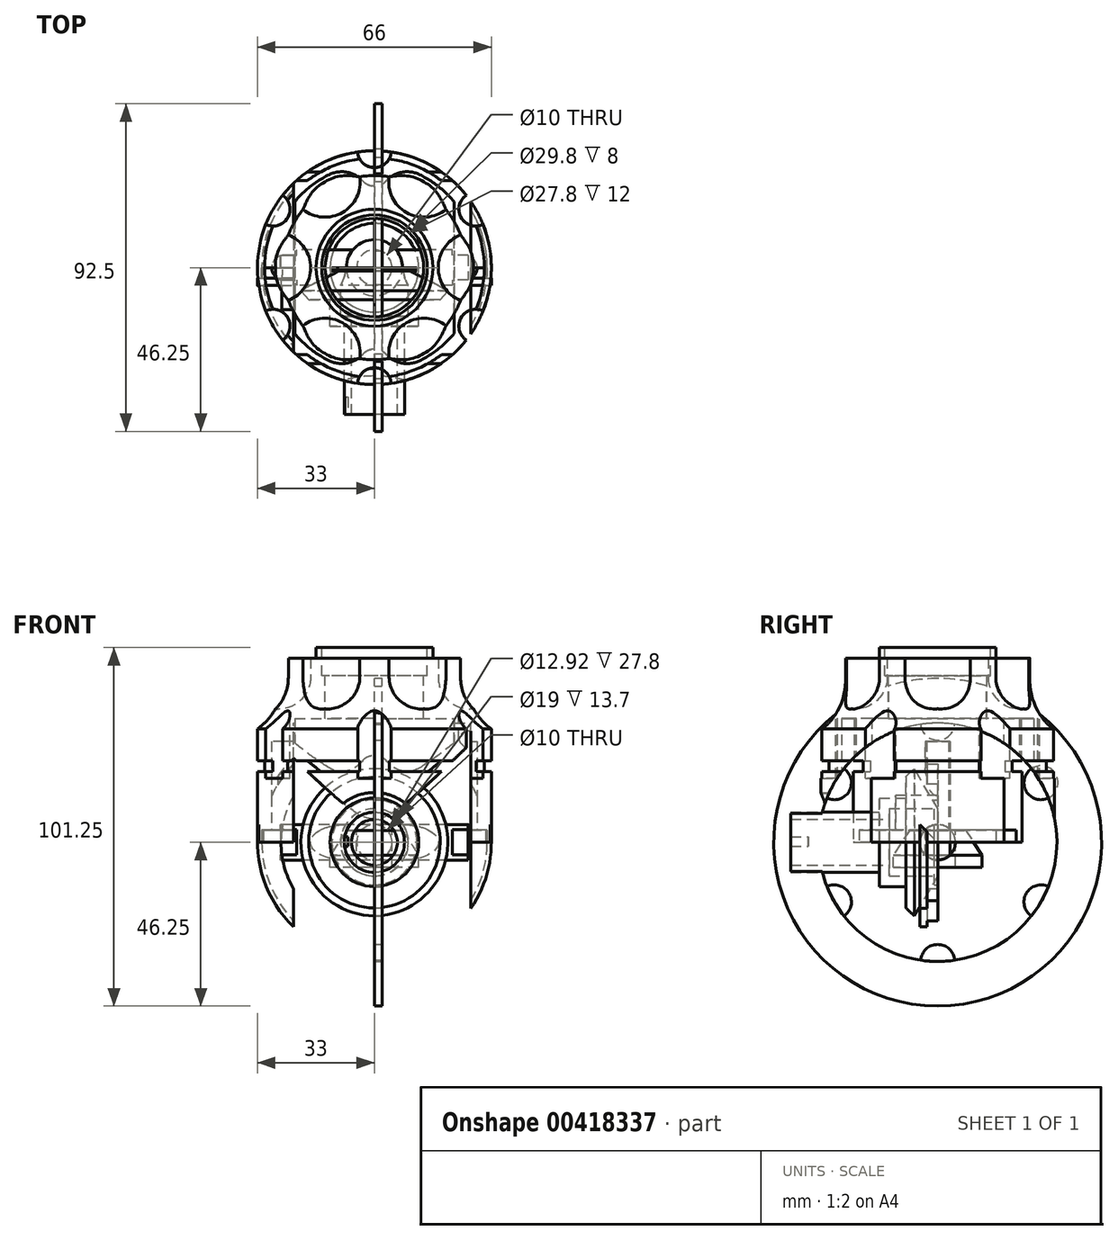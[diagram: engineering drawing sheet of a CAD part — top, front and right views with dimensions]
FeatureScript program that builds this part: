
annotation { "Feature Type Name" : "Feature", "Feature Type Description" : "" }
export const myFeature = defineFeature(function(context is Context, id is Id, definition is map)
    precondition{}
    {
        {
            var Q0;
            Q0=qCreatedBy(makeId("Top.planeOp"),FACE);
            var sketch = newSketch(context, id + "F0", { "sketchPlane" : qUnion([Q0])});
            skCircle(sketch, "E0", {"center": v(0, 0) * mm, "radius": 33 * mm});
            skSolve(sketch);
        }
        {
            var Q0;
            Q0=makeQuery(id+"F0.imprint","IMPRINT",FACE,{"disambiguationData":[TD([[makeQuery(id+"F0.imprint","IMPRINT",EDGE,{"derivedFrom":sQuery(id+"F0.wireOp",EDGE,"E0")}),1.0]])]});
            extrude(context, id + "F1", {"entities" : qUnion([Q0]), "depth" : 52 * mm});
        }
        {
            var Q0;
            Q0=qCreatedBy(makeId("Front.planeOp"),FACE);
            var sketch = newSketch(context, id + "F2", { "sketchPlane" : qUnion([Q0])});
            skFitSpline(sketch, "E1", {"points": [v(26, 52) * mm, v(26, 47.04) * mm, v(33, 32) * mm], "startDerivative": vector(0, -19.9) * mm, "endDerivative": vector(32.48, -23.97) * mm});
            skFitSpline(sketch, "E2", {"points": [v(26, 52) * mm, v(48.34, 55.62) * mm, v(50, 40.52) * mm, v(33, 32) * mm], "startDerivative": vector(76.47, 62.5) * mm, "endDerivative": vector(-112.87, -110.3) * mm});
            skLineSegment(sketch, "E3", {"start": v(33, 68.61) * mm, "end": v(33, -35.09) * mm, "construction": true});
            skLineSegment(sketch, "E4", {"start": v(26, 67.83) * mm, "end": v(26, -39.5) * mm, "construction": true});
            skLineSegment(sketch, "E5", {"start": v(-64.2, 52) * mm, "end": v(63.42, 52) * mm, "construction": true});
            skLineSegment(sketch, "E6", {"start": v(0, 62.64) * mm, "end": v(0, -36.65) * mm, "construction": true});
            skSolve(sketch);
        }
        {
            var Q0;
            Q0=makeQuery(id+"F2.imprint","IMPRINT",FACE,{"disambiguationData":[TD([[makeQuery(id+"F2.imprint","IMPRINT",EDGE,{"derivedFrom":sQuery(id+"F2.wireOp",EDGE,"E1")}),1.0]])]});
            var Q1;
            Q1=sQuery(id+"F2.wireOp",EDGE,"E6");
            revolve(context, id + "F3", {"operationType" : NewBodyOperationType.REMOVE, "entities" : qUnion([Q0]), "axis" : qUnion([Q1]), "revolveType" : RevolveType.FULL, "oppositeDirection" : true});
        }
        {
            var Q0;
            Q0=qCreatedBy(makeId("Front.planeOp"),FACE);
            var sketch = newSketch(context, id + "F4", { "sketchPlane" : qUnion([Q0])});
            skLineSegment(sketch, "E7", {"start": v(26, 80.97) * mm, "end": v(26, -38.86) * mm, "construction": true});
            skLineSegment(sketch, "E8", {"start": v(18, 70.17) * mm, "end": v(18, -34.83) * mm, "construction": true});
            skLineSegment(sketch, "E9", {"start": v(-52.24, 52) * mm, "end": v(60.82, 52) * mm, "construction": true});
            skFitSpline(sketch, "E10", {"points": [v(26, 52) * mm, v(26, 49.65) * mm, v(26, 47.35) * mm, v(26, 37.17) * mm, v(33, 32) * mm]});
            skFitSpline(sketch, "E11", {"points": [v(-33, 32) * mm, v(-26, 37.17) * mm, v(-26, 47.35) * mm, v(-26, 49.65) * mm, v(-26, 52) * mm]});
            skFitSpline(sketch, "E12", {"points": [v(26, 52) * mm, v(26, 49.65) * mm, v(26, 47.35) * mm, v(26, 37.17) * mm, v(33, 32) * mm]});
            skFitSpline(sketch, "E13", {"points": [v(-33, 32) * mm, v(-26, 37.17) * mm, v(-26, 47.35) * mm, v(-26, 49.65) * mm, v(-26, 52) * mm]});
            skLineSegment(sketch, "E14", {"start": v(18, 52) * mm, "end": v(18, 46.65) * mm});
            skPoint(sketch, "E15", {"position": v(27.95, 37.7) * mm});
            skArc(sketch, "E16", {"start": v(18, 46.65) * mm, "mid": v(20.98, 39.96) * mm, "end": v(27.95, 37.7) * mm});
            skLineSegment(sketch, "E17", {"start": v(27.95, 37.7) * mm, "end": v(27.95, 52) * mm});
            skLineSegment(sketch, "E18", {"start": v(27.95, 52) * mm, "end": v(18, 52) * mm});
            skLineSegment(sketch, "E19", {"start": v(27.95, 56.84) * mm, "end": v(27.95, 25.56) * mm, "construction": true});
            skLineSegment(sketch, "E20", {"start": v(0, 68.38) * mm, "end": v(0, -25.66) * mm, "construction": true});
            skSolve(sketch);
        }
        {
            var Q0;
            Q0 = qSketchRegion(id + "F4", true);
            var Q1;
            Q1=sQuery(id+"F4.wireOp",EDGE,"E19");
            revolve(context, id + "F5", {"entities" : qUnion([Q0]), "axis" : qUnion([Q1]), "revolveType" : RevolveType.FULL, "oppositeDirection" : true});
        }
        {
            var Q0;
            Q0=makeQuery(id+"F5.opRevolve","SWEPT_BODY",BODY,{"disambiguationData":[OSD([sQuery(id+"F4.wireOp",EDGE,"E14"),sQuery(id+"F4.wireOp",EDGE,"E16"),sQuery(id+"F4.wireOp",EDGE,"E17"),sQuery(id+"F4.wireOp",EDGE,"E18")])]});
            var Q1;
            Q1=sQuery(id+"F4.wireOp",EDGE,"E20");
            circularPattern(context, id + "F6", {"operationType" : NewBodyOperationType.REMOVE, "entities" : qUnion([Q0]), "axis" : qUnion([Q1]), "angle" : 360 * degree, "instanceCount" : 6, "equalSpace" : true});
        }
        {
            var Q0;
            Q0=qCreatedBy(makeId("Front.planeOp"),FACE);
            cPlane(context, id + "F7", {"entities" : qUnion([Q0]), "cplaneType" : CPlaneType.OFFSET, "offset" : 33 * mm, "width" : 150 * mm, "height" : 150 * mm});
        }
        {
            var Q0;
            Q0=qCreatedBy(id+"F7.planeOp",FACE);
            var sketch = newSketch(context, id + "F8", { "sketchPlane" : qUnion([Q0])});
            skLineSegment(sketch, "E21.bottom", {"start": v(0, 41.84) * mm, "end": v(4.75, 41.84) * mm});
            skLineSegment(sketch, "E21.top", {"start": v(0, 18) * mm, "end": v(4.75, 18) * mm});
            skLineSegment(sketch, "E21.left", {"start": v(0, 41.84) * mm, "end": v(0, 18) * mm});
            skLineSegment(sketch, "E21.right", {"start": v(4.75, 41.84) * mm, "end": v(4.75, 18) * mm});
            skLineSegment(sketch, "E22", {"start": v(0, 61.86) * mm, "end": v(0, -22.87) * mm, "construction": true});
            skPoint(sketch, "E22.endSnap0", {"position": v(0, 29.92) * mm});
            skSolve(sketch);
        }
        {
            var Q0;
            Q0=makeQuery(id+"F8.imprint","IMPRINT",FACE,{"disambiguationData":[TD([[makeQuery(id+"F8.imprint","IMPRINT",EDGE,{"derivedFrom":sQuery(id+"F8.wireOp",EDGE,"E21.bottom")}),-1.0]])]});
            var Q1;
            Q1=sQuery(id+"F8.wireOp",EDGE,"E22");
            revolve(context, id + "F9", {"entities" : qUnion([Q0]), "axis" : qUnion([Q1]), "revolveType" : RevolveType.FULL});
        }
        {
            var Q0;
            Q0=makeQuery(id+"F9.opRevolve","SWEPT_BODY",BODY,{"disambiguationData":[OSD([sQuery(id+"F8.wireOp",EDGE,"E21.bottom"),sQuery(id+"F8.wireOp",EDGE,"E21.top"),sQuery(id+"F8.wireOp",EDGE,"E21.left"),sQuery(id+"F8.wireOp",EDGE,"E21.right")])]});
            var Q1;
            Q1=sQuery(id+"F4.wireOp",EDGE,"E20");
            circularPattern(context, id + "F10", {"operationType" : NewBodyOperationType.REMOVE, "entities" : qUnion([Q0]), "axis" : qUnion([Q1]), "angle" : 360 * degree, "instanceCount" : 6, "equalSpace" : true});
        }
        {
            var Q0;
            Q0=qCreatedBy(makeId("Front.planeOp"),FACE);
            var sketch = newSketch(context, id + "F11", { "sketchPlane" : qUnion([Q0])});
            skLineSegment(sketch, "E23", {"start": v(33, 32) * mm, "end": v(33, 0) * mm});
            skLineSegment(sketch, "E24", {"start": v(-33, 0) * mm, "end": v(-33, 32) * mm});
            skLineSegment(sketch, "E25.bottom", {"start": v(33, 23) * mm, "end": v(31, 23) * mm});
            skLineSegment(sketch, "E25.top", {"start": v(33, 20) * mm, "end": v(31, 20) * mm});
            skLineSegment(sketch, "E25.left", {"start": v(33, 23) * mm, "end": v(33, 20) * mm});
            skLineSegment(sketch, "E25.right", {"start": v(31, 23) * mm, "end": v(31, 20) * mm});
            skSolve(sketch);
        }
        {
            var Q0;
            Q0 = qSketchRegion(id + "F11", true);
            var Q1;
            Q1=sQuery(id+"F4.wireOp",EDGE,"E20");
            revolve(context, id + "F12", {"operationType" : NewBodyOperationType.REMOVE, "entities" : qUnion([Q0]), "axis" : qUnion([Q1]), "revolveType" : RevolveType.FULL, "oppositeDirection" : true});
        }
        {
            var Q0;
            Q0=makeQuery(id+"F1.opExtrude","CAP_FACE",FACE,{"disambiguationData":[OSD([sQuery(id+"F0.wireOp",EDGE,"E0")])],"isStart":true});
            var sketch = newSketch(context, id + "F13", { "sketchPlane" : qUnion([Q0])});
            skCircle(sketch, "E26", {"center": v(0, 0) * mm, "radius": 31.8 * mm});
            skSolve(sketch);
        }
        {
            var Q0;
            Q0 = qSketchRegion(id + "F13", true);
            extrude(context, id + "F14", {"entities" : qUnion([Q0]), "operationType" : NewBodyOperationType.REMOVE, "oppositeDirection" : true, "depth" : 3.5 * mm});
        }
        {
            var Q0;
            Q0=makeQuery(id+"F14.boolean.opBoolean","COPY",FACE,{"derivedFrom":makeQuery(id+"F14.opExtrude","CAP_FACE",FACE,{"disambiguationData":[OSD([sQuery(id+"F13.wireOp",EDGE,"E26")])],"isStart":false})});
            var sketch = newSketch(context, id + "F15", { "sketchPlane" : qUnion([Q0])});
            skLineSegment(sketch, "E27", {"start": v(-22.5, 42.15) * mm, "end": v(-22.5, -45.8) * mm, "construction": true});
            skLineSegment(sketch, "E28", {"start": v(22.5, 44.15) * mm, "end": v(22.5, -45.26) * mm, "construction": true});
            skCircle(sketch, "E29", {"center": v(0, 0) * mm, "radius": 29.2 * mm, "construction": true});
            skCircle(sketch, "E30", {"center": v(0, -27.4) * mm, "radius": 4.4 * mm, "construction": true});
            skPoint(sketch, "E31", {"position": v(0, -23) * mm});
            skLineSegment(sketch, "E32", {"start": v(-22.5, 0) * mm, "end": v(22.5, 0) * mm});
            skLineSegment(sketch, "E33", {"start": v(22.5, 0) * mm, "end": v(22.5, -18.61) * mm});
            skArc(sketch, "E34", {"start": v(12.68, -26.3) * mm, "mid": v(18, -22.99) * mm, "end": v(22.5, -18.61) * mm});
            skArc(sketch, "E35", {"start": v(3.27, -24.45) * mm, "mid": v(0, -23) * mm, "end": v(-3.27, -24.45) * mm});
            skPoint(sketch, "E36.visualSharp", {"position": v(4.13, -28.9) * mm});
            skArc(sketch, "E36.filletArc", {"start": v(3.27, -24.45) * mm, "mid": v(7.67, -26.95) * mm, "end": v(12.68, -26.3) * mm});
            skLineSegment(sketch, "E37", {"start": v(-22.5, 0) * mm, "end": v(-22.5, -18.61) * mm});
            skArc(sketch, "E38", {"start": v(-22.5, -18.61) * mm, "mid": v(-18, -22.99) * mm, "end": v(-12.68, -26.3) * mm});
            skPoint(sketch, "E39.visualSharp", {"position": v(-4.13, -28.9) * mm});
            skArc(sketch, "E39.filletArc", {"start": v(-12.68, -26.3) * mm, "mid": v(-7.67, -26.95) * mm, "end": v(-3.27, -24.45) * mm});
            skSolve(sketch);
        }
        {
            var Q0;
            Q0=makeQuery(id+"F15.imprint","IMPRINT",FACE,{"disambiguationData":[TD([[makeQuery(id+"F15.imprint","IMPRINT",EDGE,{"derivedFrom":sQuery(id+"F15.wireOp",EDGE,"E32")}),-1.0]])]});
            extrude(context, id + "F16", {"entities" : qUnion([Q0]), "oppositeDirection" : true, "depth" : 31.5 * mm});
        }
        {
            var Q0;
            Q0=makeQuery(id+"F16.opExtrude","SWEPT_BODY",BODY,{"disambiguationData":[OSD([sQuery(id+"F15.wireOp",EDGE,"E32"),sQuery(id+"F15.wireOp",EDGE,"E33"),sQuery(id+"F15.wireOp",EDGE,"E34"),sQuery(id+"F15.wireOp",EDGE,"E35"),sQuery(id+"F15.wireOp",EDGE,"E36.filletArc"),sQuery(id+"F15.wireOp",EDGE,"E37"),sQuery(id+"F15.wireOp",EDGE,"E38"),sQuery(id+"F15.wireOp",EDGE,"E39.filletArc")])]});
            var Q1;
            Q1=qCreatedBy(makeId("Front.planeOp"),FACE);
            mirror(context, id + "F17", {"entities" : qUnion([Q0]), "mirrorPlane" : qUnion([Q1])});
        }
        {
            var Q0;
            Q0=makeQuery(id+"F17.opPattern","COPY",BODY,{"derivedFrom":makeQuery(id+"F16.opExtrude","SWEPT_BODY",BODY,{"disambiguationData":[OSD([sQuery(id+"F15.wireOp",EDGE,"E32"),sQuery(id+"F15.wireOp",EDGE,"E33"),sQuery(id+"F15.wireOp",EDGE,"E34"),sQuery(id+"F15.wireOp",EDGE,"E35"),sQuery(id+"F15.wireOp",EDGE,"E36.filletArc"),sQuery(id+"F15.wireOp",EDGE,"E37"),sQuery(id+"F15.wireOp",EDGE,"E38"),sQuery(id+"F15.wireOp",EDGE,"E39.filletArc")])]}),"instanceName":"1"});
            var Q1;
            Q1=makeQuery(id+"F16.opExtrude","SWEPT_BODY",BODY,{"disambiguationData":[OSD([sQuery(id+"F15.wireOp",EDGE,"E32"),sQuery(id+"F15.wireOp",EDGE,"E33"),sQuery(id+"F15.wireOp",EDGE,"E34"),sQuery(id+"F15.wireOp",EDGE,"E35"),sQuery(id+"F15.wireOp",EDGE,"E36.filletArc"),sQuery(id+"F15.wireOp",EDGE,"E37"),sQuery(id+"F15.wireOp",EDGE,"E38"),sQuery(id+"F15.wireOp",EDGE,"E39.filletArc")])]});
            var Q2;
            Q2=makeQuery(id+"F1.opExtrude","SWEPT_BODY",BODY,{"disambiguationData":[OSD([sQuery(id+"F0.wireOp",EDGE,"E0")])]});
            booleanBodies(context, id + "F18", {"operationType" : BooleanOperationType.SUBTRACTION, "tools" : qUnion([Q0, Q1]), "targets" : qUnion([Q2])});
        }
        {
            var Q0;
            Q0=makeQuery(id+"F14.boolean.opBoolean","COPY",FACE,{"derivedFrom":makeQuery(id+"F14.opExtrude","CAP_FACE",FACE,{"disambiguationData":[OSD([sQuery(id+"F13.wireOp",EDGE,"E26")])],"isStart":false})});
            var sketch = newSketch(context, id + "F19", { "sketchPlane" : qUnion([Q0])});
            skLineSegment(sketch, "E40.bottom", {"start": v(-22.5, 3.5) * mm, "end": v(-25.5, 3.5) * mm});
            skLineSegment(sketch, "E40.top", {"start": v(-22.5, -3.5) * mm, "end": v(-25.5, -3.5) * mm});
            skLineSegment(sketch, "E40.left", {"start": v(-22.5, 3.5) * mm, "end": v(-22.5, -3.5) * mm});
            skLineSegment(sketch, "E40.right", {"start": v(-25.5, 3.5) * mm, "end": v(-25.5, -3.5) * mm, "construction": true});
            skCircle(sketch, "E41", {"center": v(-25.5, 0) * mm, "radius": 3.5 * mm, "construction": true});
            skPoint(sketch, "E42", {"position": v(-29, 0) * mm});
            skArc(sketch, "E43", {"start": v(-25.5, 3.5) * mm, "mid": v(-29, 0) * mm, "end": v(-25.5, -3.5) * mm});
            skSolve(sketch);
        }
        {
            var Q0;
            Q0=makeQuery(id+"F19.imprint","IMPRINT",FACE,{"disambiguationData":[TD([[makeQuery(id+"F19.imprint","IMPRINT",EDGE,{"derivedFrom":sQuery(id+"F19.wireOp",EDGE,"E40.bottom")}),1.0]])]});
            extrude(context, id + "F20", {"entities" : qUnion([Q0]), "oppositeDirection" : true, "depth" : 25 * mm});
        }
        {
            var Q0;
            Q0=makeQuery(id+"F20.opExtrude","SWEPT_BODY",BODY,{"disambiguationData":[OSD([sQuery(id+"F19.wireOp",EDGE,"E40.bottom"),sQuery(id+"F19.wireOp",EDGE,"E40.top"),sQuery(id+"F19.wireOp",EDGE,"E40.left"),sQuery(id+"F19.wireOp",EDGE,"E43")])]});
            var Q1;
            Q1=qCreatedBy(makeId("Right.planeOp"),FACE);
            mirror(context, id + "F21", {"entities" : qUnion([Q0]), "mirrorPlane" : qUnion([Q1])});
        }
        {
            var Q0;
            Q0=makeQuery(id+"F20.opExtrude","SWEPT_BODY",BODY,{"disambiguationData":[OSD([sQuery(id+"F19.wireOp",EDGE,"E40.bottom"),sQuery(id+"F19.wireOp",EDGE,"E40.top"),sQuery(id+"F19.wireOp",EDGE,"E40.left"),sQuery(id+"F19.wireOp",EDGE,"E43")])]});
            var Q1;
            Q1=makeQuery(id+"F21.opPattern","COPY",BODY,{"derivedFrom":makeQuery(id+"F20.opExtrude","SWEPT_BODY",BODY,{"disambiguationData":[OSD([sQuery(id+"F19.wireOp",EDGE,"E40.bottom"),sQuery(id+"F19.wireOp",EDGE,"E40.top"),sQuery(id+"F19.wireOp",EDGE,"E40.left"),sQuery(id+"F19.wireOp",EDGE,"E43")])]}),"instanceName":"1"});
            var Q2;
            Q2=makeQuery(id+"F1.opExtrude","SWEPT_BODY",BODY,{"disambiguationData":[OSD([sQuery(id+"F0.wireOp",EDGE,"E0")])]});
            booleanBodies(context, id + "F22", {"operationType" : BooleanOperationType.SUBTRACTION, "tools" : qUnion([Q0, Q1]), "targets" : qUnion([Q2])});
        }
        {
            var Q0;
            Q0=makeQuery(id+"F1.opExtrude","CAP_FACE",FACE,{"disambiguationData":[OSD([sQuery(id+"F0.wireOp",EDGE,"E0")])],"isStart":false});
            var sketch = newSketch(context, id + "F23", { "sketchPlane" : qUnion([Q0])});
            skCircle(sketch, "E44", {"center": v(0, 0) * mm, "radius": 14.9 * mm});
            skSolve(sketch);
        }
        {
            var Q0;
            Q0=makeQuery(id+"F23.imprint","IMPRINT",FACE,{"disambiguationData":[TD([[makeQuery(id+"F23.imprint","IMPRINT",EDGE,{"derivedFrom":sQuery(id+"F23.wireOp",EDGE,"E44")}),1.0]])]});
            extrude(context, id + "F24", {"entities" : qUnion([Q0]), "operationType" : NewBodyOperationType.REMOVE, "oppositeDirection" : true, "depth" : 5 * mm});
        }
        {
            var Q0;
            Q0=makeQuery(id+"F1.opExtrude","CAP_FACE",FACE,{"disambiguationData":[OSD([sQuery(id+"F0.wireOp",EDGE,"E0")])],"isStart":false});
            var sketch = newSketch(context, id + "F25", { "sketchPlane" : qUnion([Q0])});
            skCircle(sketch, "E45", {"center": v(0, 0) * mm, "radius": 14.9 * mm});
            skCircle(sketch, "E46", {"center": v(0, 0) * mm, "radius": 16.5 * mm});
            skSolve(sketch);
        }
        {
            var Q0;
            Q0 = qSketchRegion(id + "F25", true);
            extrude(context, id + "F26", {"entities" : qUnion([Q0]), "operationType" : NewBodyOperationType.ADD, "depth" : 3 * mm});
        }
        {
            var Q0;
            Q0=makeQuery(id+"F24.boolean.opBoolean","COPY",FACE,{"derivedFrom":makeQuery(id+"F24.opExtrude","CAP_FACE",FACE,{"disambiguationData":[OSD([sQuery(id+"F23.wireOp",EDGE,"E44")])],"isStart":false})});
            var sketch = newSketch(context, id + "F27", { "sketchPlane" : qUnion([Q0])});
            skCircle(sketch, "E47", {"center": v(0, 0) * mm, "radius": 13.9 * mm});
            skSolve(sketch);
        }
        {
            var Q0;
            Q0 = qSketchRegion(id + "F27", true);
            extrude(context, id + "F28", {"entities" : qUnion([Q0]), "operationType" : NewBodyOperationType.REMOVE, "oppositeDirection" : true, "depth" : 25 * mm, "hasSecondDirection" : true, "secondDirectionOppositeDirection" : false, "secondDirectionDepth" : 25 * mm});
        }
        {
            var Q0;
            Q0=qCreatedBy(makeId("Front.planeOp"),FACE);
            var sketch = newSketch(context, id + "F29", { "sketchPlane" : qUnion([Q0])});
            skCircle(sketch, "E48", {"center": v(0, 0) * mm, "radius": 31.8 * mm});
            skSolve(sketch);
        }
        {
            var Q0;
            Q0=makeQuery(id+"F29.imprint","IMPRINT",FACE,{"disambiguationData":[TD([[makeQuery(id+"F29.imprint","IMPRINT",EDGE,{"derivedFrom":sQuery(id+"F29.wireOp",EDGE,"E48")}),1.0]])]});
            extrude(context, id + "F30", {"entities" : qUnion([Q0]), "depth" : 3 * mm});
        }
        {
            var Q0;
            Q0=makeQuery(id+"F30.opExtrude","CAP_FACE",FACE,{"disambiguationData":[OSD([sQuery(id+"F29.wireOp",EDGE,"E48")])],"isStart":false});
            var sketch = newSketch(context, id + "F31", { "sketchPlane" : qUnion([Q0])});
            skCircle(sketch, "E49", {"center": v(0, 0) * mm, "radius": 33 * mm});
            skSolve(sketch);
        }
        {
            var Q0;
            Q0 = qSketchRegion(id + "F31", true);
            extrude(context, id + "F32", {"entities" : qUnion([Q0]), "operationType" : NewBodyOperationType.ADD, "depth" : 2 * mm});
        }
        {
            var Q0;
            Q0=makeQuery(id+"F32.opExtrude","CAP_FACE",FACE,{"disambiguationData":[OSD([sQuery(id+"F31.wireOp",EDGE,"E49")])],"isStart":false});
            var sketch = newSketch(context, id + "F33", { "sketchPlane" : qUnion([Q0])});
            skCircle(sketch, "E50", {"center": v(0, 0) * mm, "radius": 19 * mm});
            skSolve(sketch);
        }
        {
            var Q0;
            Q0 = qSketchRegion(id + "F33", true);
            extrude(context, id + "F34", {"entities" : qUnion([Q0]), "operationType" : NewBodyOperationType.ADD, "depth" : 4.5 * mm});
        }
        {
            var Q0;
            Q0=makeQuery(id+"F34.opExtrude","CAP_FACE",FACE,{"disambiguationData":[OSD([sQuery(id+"F33.wireOp",EDGE,"E50")])],"isStart":false});
            var sketch = newSketch(context, id + "F35", { "sketchPlane" : qUnion([Q0])});
            skCircle(sketch, "E51", {"center": v(0, 0) * mm, "radius": 17.35 * mm});
            skSolve(sketch);
        }
        {
            var Q0;
            Q0=makeQuery(id+"F35.imprint","IMPRINT",FACE,{"disambiguationData":[TD([[makeQuery(id+"F35.imprint","IMPRINT",EDGE,{"derivedFrom":sQuery(id+"F35.wireOp",EDGE,"E51")}),1.0]])]});
            extrude(context, id + "F36", {"entities" : qUnion([Q0]), "operationType" : NewBodyOperationType.ADD, "depth" : 10.4 * mm});
        }
        {
            var Q0;
            Q0=makeQuery(id+"F36.opExtrude","CAP_FACE",FACE,{"disambiguationData":[OSD([sQuery(id+"F35.wireOp",EDGE,"E51")])],"isStart":false});
            var sketch = newSketch(context, id + "F37", { "sketchPlane" : qUnion([Q0])});
            skCircle(sketch, "E52", {"center": v(0, 0) * mm, "radius": 15.05 * mm});
            skSolve(sketch);
        }
        {
            var Q0;
            Q0=makeQuery(id+"F37.imprint","IMPRINT",FACE,{"disambiguationData":[TD([[makeQuery(id+"F37.imprint","IMPRINT",EDGE,{"derivedFrom":sQuery(id+"F37.wireOp",EDGE,"E52")}),1.0]])]});
            extrude(context, id + "F38", {"entities" : qUnion([Q0]), "operationType" : NewBodyOperationType.REMOVE, "oppositeDirection" : true, "depth" : 8.5 * mm});
        }
        {
            var Q0;
            Q0=makeQuery(id+"F38.boolean.opBoolean","COPY",FACE,{"derivedFrom":makeQuery(id+"F38.opExtrude","CAP_FACE",FACE,{"disambiguationData":[OSD([sQuery(id+"F37.wireOp",EDGE,"E52")])],"isStart":false})});
            var sketch = newSketch(context, id + "F39", { "sketchPlane" : qUnion([Q0])});
            skCircle(sketch, "E53", {"center": v(0, 0) * mm, "radius": 14.05 * mm});
            skSolve(sketch);
        }
        {
            var Q0;
            Q0=makeQuery(id+"F39.imprint","IMPRINT",FACE,{"disambiguationData":[TD([[makeQuery(id+"F39.imprint","IMPRINT",EDGE,{"derivedFrom":sQuery(id+"F39.wireOp",EDGE,"E53")}),1.0]])]});
            extrude(context, id + "F40", {"entities" : qUnion([Q0]), "operationType" : NewBodyOperationType.REMOVE, "depth" : 25 * mm, "hasSecondDirection" : true, "secondDirectionOppositeDirection" : true, "secondDirectionDepth" : 25 * mm});
        }
        {
            var Q0;
            Q0=qCreatedBy(makeId("Right.planeOp"),FACE);
            var sketch = newSketch(context, id + "F41", { "sketchPlane" : qUnion([Q0])});
            skCircle(sketch, "E54", {"center": v(0, 0) * mm, "radius": 46.25 * mm});
            skSolve(sketch);
        }
        {
            var Q0;
            Q0=makeQuery(id+"F41.imprint","IMPRINT",FACE,{"disambiguationData":[TD([[makeQuery(id+"F41.imprint","IMPRINT",EDGE,{"derivedFrom":sQuery(id+"F41.wireOp",EDGE,"E54")}),1.0]])]});
            extrude(context, id + "F42", {"entities" : qUnion([Q0]), "depth" : 2.2 * mm});
        }
        {
            var Q0;
            Q0=makeQuery(id+"F42.opExtrude","CAP_FACE",FACE,{"disambiguationData":[OSD([sQuery(id+"F41.wireOp",EDGE,"E54")])],"isStart":false});
            var sketch = newSketch(context, id + "F43", { "sketchPlane" : qUnion([Q0])});
            skCircle(sketch, "E55", {"center": v(0, 0) * mm, "radius": 33.65 * mm});
            skSolve(sketch);
        }
        {
            var Q0;
            Q0 = qSketchRegion(id + "F43", true);
            extrude(context, id + "F44", {"entities" : qUnion([Q0]), "operationType" : NewBodyOperationType.REMOVE, "oppositeDirection" : true, "depth" : 25 * mm, "hasSecondDirection" : true, "secondDirectionOppositeDirection" : false, "secondDirectionDepth" : 25 * mm});
        }
        {
            var Q0;
            Q0=makeQuery(id+"F42.opExtrude","CAP_FACE",FACE,{"disambiguationData":[OSD([sQuery(id+"F41.wireOp",EDGE,"E54")])],"isStart":false});
            var sketch = newSketch(context, id + "F45", { "sketchPlane" : qUnion([Q0])});
            skCircle(sketch, "E56", {"center": v(0, 33.65) * mm, "radius": 4.8 * mm, "construction": true});
            skArc(sketch, "E57", {"start": v(-4.79, 33.3) * mm, "mid": v(0, 33.65) * mm, "end": v(4.79, 33.3) * mm});
            skArc(sketch, "E58", {"start": v(-4.79, 33.3) * mm, "mid": v(0, 28.85) * mm, "end": v(4.79, 33.3) * mm});
            skSolve(sketch);
        }
        {
            var Q0;
            Q0 = qSketchRegion(id + "F45", true);
            extrude(context, id + "F46", {"entities" : qUnion([Q0]), "oppositeDirection" : true, "depth" : 2.2 * mm});
        }
        {
            var Q0;
            Q0=qCreatedBy(makeId("Front.planeOp"),FACE);
            var sketch = newSketch(context, id + "F47", { "sketchPlane" : qUnion([Q0])});
            skLineSegment(sketch, "E59", {"start": v(-62.78, 0) * mm, "end": v(62.78, 0) * mm, "construction": true});
            skSolve(sketch);
        }
        {
            var Q0;
            Q0=makeQuery(id+"F46.opExtrude","SWEPT_BODY",BODY,{"disambiguationData":[OSD([sQuery(id+"F45.wireOp",EDGE,"E57"),sQuery(id+"F45.wireOp",EDGE,"E58")])]});
            var Q1;
            Q1=sQuery(id+"F47.wireOp",EDGE,"E59");
            circularPattern(context, id + "F48", {"entities" : qUnion([Q0]), "axis" : qUnion([Q1]), "angle" : 360 * degree, "instanceCount" : 6, "equalSpace" : true});
        }
        {
            var Q0;
            Q0=qCreatedBy(makeId("Front.planeOp"),FACE);
            var sketch = newSketch(context, id + "F49", { "sketchPlane" : qUnion([Q0])});
            skCircle(sketch, "E60", {"center": v(0, 0) * mm, "radius": 23 * mm});
            skSolve(sketch);
        }
        {
            var Q0;
            Q0=makeQuery(id+"F49.imprint","IMPRINT",FACE,{"disambiguationData":[TD([[makeQuery(id+"F49.imprint","IMPRINT",EDGE,{"derivedFrom":sQuery(id+"F49.wireOp",EDGE,"E60")}),1.0]])]});
            extrude(context, id + "F50", {"entities" : qUnion([Q0]), "depth" : 9 * mm});
        }
        {
            var Q0;
            Q0=makeQuery(id+"F50.opExtrude","CAP_FACE",FACE,{"disambiguationData":[OSD([sQuery(id+"F49.wireOp",EDGE,"E60")])],"isStart":false});
            var sketch = newSketch(context, id + "F51", { "sketchPlane" : qUnion([Q0])});
            skCircle(sketch, "E61", {"center": v(0, 0) * mm, "radius": 12.5 * mm});
            skSolve(sketch);
        }
        {
            var Q0;
            Q0=makeQuery(id+"F51.imprint","IMPRINT",FACE,{"disambiguationData":[TD([[makeQuery(id+"F51.imprint","IMPRINT",EDGE,{"derivedFrom":sQuery(id+"F51.wireOp",EDGE,"E61")}),1.0]])]});
            extrude(context, id + "F52", {"entities" : qUnion([Q0]), "operationType" : NewBodyOperationType.ADD, "depth" : 7.5 * mm});
        }
        {
            var Q0;
            Q0=makeQuery(id+"F52.opExtrude","CAP_FACE",FACE,{"disambiguationData":[OSD([sQuery(id+"F51.wireOp",EDGE,"E61")])],"isStart":false});
            var sketch = newSketch(context, id + "F53", { "sketchPlane" : qUnion([Q0])});
            skCircle(sketch, "E62", {"center": v(0, 0) * mm, "radius": 8.5 * mm});
            skSolve(sketch);
        }
        {
            var Q0;
            Q0=makeQuery(id+"F53.imprint","IMPRINT",FACE,{"disambiguationData":[TD([[makeQuery(id+"F53.imprint","IMPRINT",EDGE,{"derivedFrom":sQuery(id+"F53.wireOp",EDGE,"E62")}),1.0]])]});
            extrude(context, id + "F54", {"entities" : qUnion([Q0]), "operationType" : NewBodyOperationType.ADD, "depth" : 25 * mm});
        }
        {
            var Q0;
            Q0=qCreatedBy(makeId("Right.planeOp"),FACE);
            var sketch = newSketch(context, id + "F55", { "sketchPlane" : qUnion([Q0])});
            skLineSegment(sketch, "E63", {"start": v(0, -23) * mm, "end": v(-9, -23) * mm});
            skLineSegment(sketch, "E64", {"start": v(33.63, 0) * mm, "end": v(-49.1, 0) * mm, "construction": true});
            skLineSegment(sketch, "E65", {"start": v(-46.93, 20.75) * mm, "end": v(42.33, 20.75) * mm, "construction": true});
            skLineSegment(sketch, "E66", {"start": v(0, 9.5) * mm, "end": v(-6.58, 20.75) * mm});
            skLineSegment(sketch, "E67", {"start": v(0, 9.5) * mm, "end": v(0, 26.35) * mm});
            skLineSegment(sketch, "E68", {"start": v(0, 26.35) * mm, "end": v(-11.85, 26.35) * mm});
            skLineSegment(sketch, "E69", {"start": v(-11.85, 26.35) * mm, "end": v(-11.85, 20.75) * mm});
            skLineSegment(sketch, "E70", {"start": v(-10.3, 17.35) * mm, "end": v(-6.58, 20.75) * mm});
            skLineSegment(sketch, "E71", {"start": v(-10.3, 17.35) * mm, "end": v(-11.85, 20.75) * mm});
            skSolve(sketch);
        }
        {
            var Q0;
            Q0=makeQuery(id+"F55.imprint","IMPRINT",FACE,{"disambiguationData":[TD([[makeQuery(id+"F55.imprint","IMPRINT",EDGE,{"derivedFrom":sQuery(id+"F55.wireOp",EDGE,"E66")}),-1.0]])]});
            var Q1;
            Q1=sQuery(id+"F55.wireOp",EDGE,"E64");
            revolve(context, id + "F56", {"operationType" : NewBodyOperationType.REMOVE, "entities" : qUnion([Q0]), "axis" : qUnion([Q1]), "revolveType" : RevolveType.FULL, "oppositeDirection" : true});
        }
        {
            var Q0;
            Q0=makeQuery(id+"F50.opExtrude","CAP_FACE",FACE,{"disambiguationData":[OSD([sQuery(id+"F49.wireOp",EDGE,"E60")])],"isStart":true});
            var sketch = newSketch(context, id + "F57", { "sketchPlane" : qUnion([Q0])});
            skCircle(sketch, "E72", {"center": v(0, 0) * mm, "radius": 9.5 * mm});
            skSolve(sketch);
        }
        {
            var Q0;
            Q0=makeQuery(id+"F57.imprint","IMPRINT",FACE,{"disambiguationData":[TD([[makeQuery(id+"F57.imprint","IMPRINT",EDGE,{"derivedFrom":sQuery(id+"F57.wireOp",EDGE,"E72")}),-1.0]])]});
            extrude(context, id + "F58", {"entities" : qUnion([Q0]), "operationType" : NewBodyOperationType.REMOVE, "oppositeDirection" : true, "depth" : 13.7 * mm});
        }
        {
            var Q0;
            Q0=makeQuery(id+"F58.boolean.opBoolean","COPY",FACE,{"derivedFrom":makeQuery(id+"F58.opExtrude","CAP_FACE",FACE,{"disambiguationData":[OSD([sQuery(id+"F57.wireOp",EDGE,"E72")])],"isStart":false})});
            var sketch = newSketch(context, id + "F59", { "sketchPlane" : qUnion([Q0])});
            skCircle(sketch, "E73", {"center": v(0, 0) * mm, "radius": 6.46 * mm});
            skSolve(sketch);
        }
        {
            var Q0;
            Q0=makeQuery(id+"F59.imprint","IMPRINT",FACE,{"disambiguationData":[TD([[makeQuery(id+"F59.imprint","IMPRINT",EDGE,{"derivedFrom":sQuery(id+"F59.wireOp",EDGE,"E73")}),1.0]])]});
            var Q1;
            Q1=makeQuery(id+"F54.opExtrude","CAP_FACE",FACE,{"disambiguationData":[OSD([sQuery(id+"F53.wireOp",EDGE,"E62")])],"isStart":false});
            extrude(context, id + "F60", {"entities" : qUnion([Q0]), "operationType" : NewBodyOperationType.REMOVE, "endBound" : BoundingType.UP_TO_SURFACE, "oppositeDirection" : true, "endBoundEntityFace" : qUnion([Q1]), "depth" : 25 * mm});
        }
        {
            var Q0;
            Q0=qCreatedBy(makeId("Right.planeOp"),FACE);
            var sketch = newSketch(context, id + "F61", { "sketchPlane" : qUnion([Q0])});
            skCircle(sketch, "E74", {"center": v(0, 0) * mm, "radius": 5 * mm});
            skSolve(sketch);
        }
        {
            var Q0;
            Q0=makeQuery(id+"F61.imprint","IMPRINT",FACE,{"disambiguationData":[TD([[makeQuery(id+"F61.imprint","IMPRINT",EDGE,{"derivedFrom":sQuery(id+"F61.wireOp",EDGE,"E74")}),1.0]])]});
            extrude(context, id + "F62", {"entities" : qUnion([Q0]), "depth" : 26.5 * mm});
        }
        {
            var Q0;
            Q0=makeQuery(id+"F62.opExtrude","CAP_FACE",FACE,{"disambiguationData":[OSD([sQuery(id+"F61.wireOp",EDGE,"E74")])],"isStart":false});
            var sketch = newSketch(context, id + "F63", { "sketchPlane" : qUnion([Q0])});
            skLineSegment(sketch, "E75.bottom", {"start": v(5.37, 4.4) * mm, "end": v(3.5, 4.4) * mm});
            skLineSegment(sketch, "E75.top", {"start": v(5.37, -5) * mm, "end": v(3.5, -5) * mm});
            skLineSegment(sketch, "E75.left", {"start": v(5.37, 4.4) * mm, "end": v(5.37, -5) * mm});
            skLineSegment(sketch, "E75.right", {"start": v(3.5, 4.4) * mm, "end": v(3.5, -5) * mm});
            skSolve(sketch);
        }
        {
            var Q0;
            Q0 = qSketchRegion(id + "F63", true);
            extrude(context, id + "F64", {"entities" : qUnion([Q0]), "oppositeDirection" : true, "depth" : 4.5 * mm});
        }
        {
            var Q0;
            Q0=makeQuery(id+"F64.opExtrude","SWEPT_BODY",BODY,{"disambiguationData":[OSD([sQuery(id+"F63.wireOp",EDGE,"E75.bottom"),sQuery(id+"F63.wireOp",EDGE,"E75.top"),sQuery(id+"F63.wireOp",EDGE,"E75.left"),sQuery(id+"F63.wireOp",EDGE,"E75.right")])]});
            var Q1;
            Q1=qCreatedBy(makeId("Front.planeOp"),FACE);
            mirror(context, id + "F65", {"entities" : qUnion([Q0]), "mirrorPlane" : qUnion([Q1])});
        }
        {
            var Q0;
            Q0=makeQuery(id+"F65.opPattern","COPY",BODY,{"derivedFrom":makeQuery(id+"F64.opExtrude","SWEPT_BODY",BODY,{"disambiguationData":[OSD([sQuery(id+"F63.wireOp",EDGE,"E75.bottom"),sQuery(id+"F63.wireOp",EDGE,"E75.top"),sQuery(id+"F63.wireOp",EDGE,"E75.left"),sQuery(id+"F63.wireOp",EDGE,"E75.right")])]}),"instanceName":"1"});
            var Q1;
            Q1=makeQuery(id+"F64.opExtrude","SWEPT_BODY",BODY,{"disambiguationData":[OSD([sQuery(id+"F63.wireOp",EDGE,"E75.bottom"),sQuery(id+"F63.wireOp",EDGE,"E75.top"),sQuery(id+"F63.wireOp",EDGE,"E75.left"),sQuery(id+"F63.wireOp",EDGE,"E75.right")])]});
            var Q2;
            Q2=makeQuery(id+"F62.opExtrude","SWEPT_BODY",BODY,{"disambiguationData":[OSD([sQuery(id+"F61.wireOp",EDGE,"E74")])]});
            booleanBodies(context, id + "F66", {"operationType" : BooleanOperationType.SUBTRACTION, "tools" : qUnion([Q0, Q1]), "targets" : qUnion([Q2])});
        }
        {
            var Q0;
            Q0=makeQuery(id+"F62.opExtrude","SWEPT_BODY",BODY,{"disambiguationData":[OSD([sQuery(id+"F61.wireOp",EDGE,"E74")])]});
            var Q1;
            Q1=qCreatedBy(makeId("Right.planeOp"),FACE);
            mirror(context, id + "F67", {"operationType" : NewBodyOperationType.ADD, "entities" : qUnion([Q0]), "mirrorPlane" : qUnion([Q1])});
        }
        {
            var Q0;
            Q0=qCreatedBy(makeId("Right.planeOp"),FACE);
            var sketch = newSketch(context, id + "F68", { "sketchPlane" : qUnion([Q0])});
            skLineSegment(sketch, "E76", {"start": v(5, 3.39) * mm, "end": v(5, -7.11) * mm});
            skLineSegment(sketch, "E77", {"start": v(5, -7.11) * mm, "end": v(12.5, -7.11) * mm});
            skLineSegment(sketch, "E78", {"start": v(12.5, -7.11) * mm, "end": v(12.5, -3.61) * mm});
            skLineSegment(sketch, "E79", {"start": v(12.5, -3.61) * mm, "end": v(7.9, 3.39) * mm});
            skLineSegment(sketch, "E80", {"start": v(7.9, 3.39) * mm, "end": v(5, 3.39) * mm});
            skLineSegment(sketch, "E81", {"start": v(0, 17.26) * mm, "end": v(0, -22.84) * mm, "construction": true});
            skSolve(sketch);
        }
        {
            var Q0;
            Q0 = qSketchRegion(id + "F68", true);
            var Q1;
            Q1=sQuery(id+"F68.wireOp",EDGE,"E81");
            revolve(context, id + "F69", {"entities" : qUnion([Q0]), "axis" : qUnion([Q1]), "revolveType" : RevolveType.FULL});
        }
        {
            var Q0;
            Q0=qCreatedBy(makeId("Front.planeOp"),FACE);
            var sketch = newSketch(context, id + "F70", { "sketchPlane" : qUnion([Q0])});
            skCircle(sketch, "E82", {"center": v(0, 0) * mm, "radius": 5 * mm});
            skCircle(sketch, "E83", {"center": v(0, 0) * mm, "radius": 12 * mm});
            skSolve(sketch);
        }
        {
            var Q0;
            Q0=makeQuery(id+"F70.imprint","IMPRINT",FACE,{"disambiguationData":[TD([[makeQuery(id+"F70.imprint","IMPRINT",EDGE,{"derivedFrom":sQuery(id+"F70.wireOp",EDGE,"E82")}),-1.0]])]});
            extrude(context, id + "F71", {"entities" : qUnion([Q0]), "depth" : 0.9 * mm});
        }
        {
            var Q0;
            Q0=makeQuery(id+"F54.opExtrude","CAP_FACE",FACE,{"disambiguationData":[OSD([sQuery(id+"F53.wireOp",EDGE,"E62")])],"isStart":false});
            var sketch = newSketch(context, id + "F72", { "sketchPlane" : qUnion([Q0])});
            skLineSegment(sketch, "E84.bottom", {"start": v(-10.19, -1.13) * mm, "end": v(-7.43, -1.13) * mm});
            skLineSegment(sketch, "E84.top", {"start": v(-10.19, 1.5) * mm, "end": v(-7.43, 1.5) * mm});
            skLineSegment(sketch, "E84.left", {"start": v(-10.19, -1.13) * mm, "end": v(-10.19, 1.5) * mm});
            skLineSegment(sketch, "E84.right", {"start": v(-7.43, -1.13) * mm, "end": v(-7.43, 1.5) * mm});
            skLineSegment(sketch, "E85.bottom", {"start": v(-10.19, 1.5) * mm, "end": v(-10.19, 1.5) * mm});
            skLineSegment(sketch, "E85.top", {"start": v(-10.19, 0.18) * mm, "end": v(-10.19, 0.18) * mm});
            skLineSegment(sketch, "E85.left", {"start": v(-10.19, 1.5) * mm, "end": v(-10.19, 0.18) * mm});
            skLineSegment(sketch, "E85.right", {"start": v(-10.19, 1.5) * mm, "end": v(-10.19, 0.18) * mm});
            skSolve(sketch);
        }
        {
            var Q0;
            Q0 = qSketchRegion(id + "F72", true);
            extrude(context, id + "F73", {"entities" : qUnion([Q0]), "operationType" : NewBodyOperationType.REMOVE, "oppositeDirection" : true, "depth" : 5 * mm});
        }
    });
